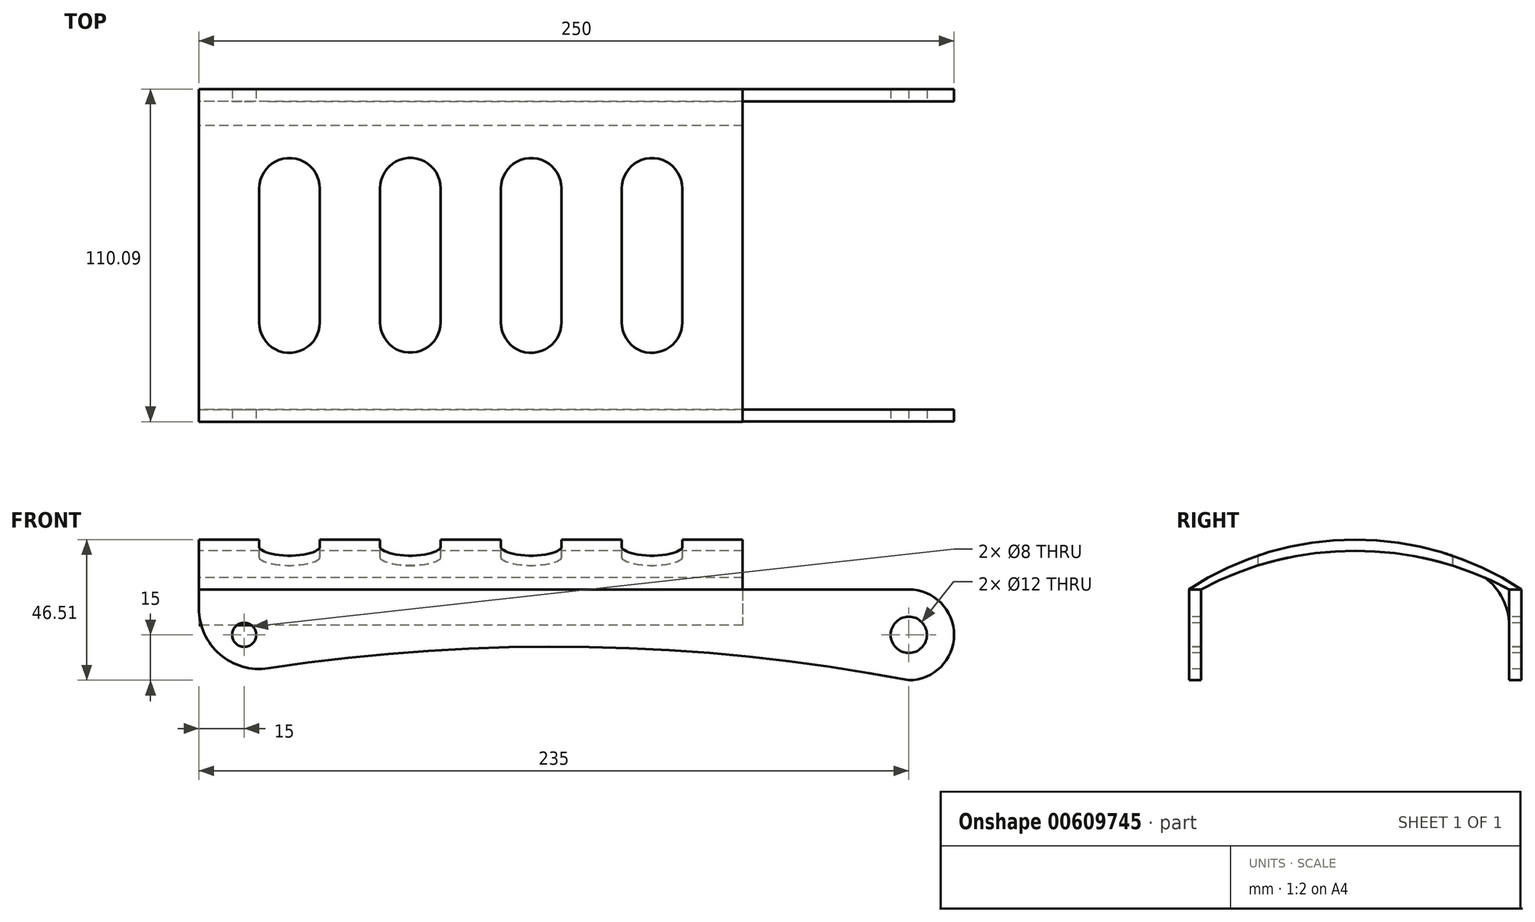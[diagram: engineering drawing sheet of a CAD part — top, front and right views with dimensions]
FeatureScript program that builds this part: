
annotation { "Feature Type Name" : "Feature", "Feature Type Description" : "" }
export const myFeature = defineFeature(function(context is Context, id is Id, definition is map)
    precondition{}
    {
        {
            var Q0;
            Q0=qCreatedBy(makeId("Top.planeOp"),FACE);
            var sketch = newSketch(context, id + "F0", { "sketchPlane" : qUnion([Q0])});
            skLineSegment(sketch, "E0.bottom", {"start": v(-125, 84.4) * mm, "end": v(125, 84.4) * mm});
            skLineSegment(sketch, "E0.top", {"start": v(-125, 80.4) * mm, "end": v(125, 80.4) * mm});
            skLineSegment(sketch, "E0.left", {"start": v(-125, 84.4) * mm, "end": v(-125, 80.4) * mm});
            skLineSegment(sketch, "E0.right", {"start": v(125, 84.4) * mm, "end": v(125, 80.4) * mm});
            skLineSegment(sketch, "E1.bottom", {"start": v(-125, -21.6) * mm, "end": v(125, -21.6) * mm});
            skLineSegment(sketch, "E1.top", {"start": v(-125, -25.6) * mm, "end": v(125, -25.6) * mm});
            skLineSegment(sketch, "E1.left", {"start": v(-125, -21.6) * mm, "end": v(-125, -25.6) * mm});
            skLineSegment(sketch, "E1.right", {"start": v(125, -21.6) * mm, "end": v(125, -25.6) * mm});
            skSolve(sketch);
        }
        {
            var Q0;
            Q0 = qSketchRegion(id + "F0", true);
            extrude(context, id + "F1", {"entities" : qUnion([Q0]), "depth" : 30 * mm, "offsetDistance" : 25 * mm});
        }
        {
            var Q0;
            Q0=makeQuery(id+"F1.opExtrude","SWEPT_FACE",FACE,{"disambiguationData":[OSD([sQuery(id+"F0.wireOp",EDGE,"E1.top")])]});
            var sketch = newSketch(context, id + "F2", { "sketchPlane" : qUnion([Q0])});
            skLineSegment(sketch, "E2", {"start": v(110, 37.38) * mm, "end": v(110, -21.55) * mm, "construction": true});
            skArc(sketch, "E3", {"start": v(110, 0) * mm, "mid": v(125, 15) * mm, "end": v(110, 30) * mm});
            skArc(sketch, "E4", {"start": v(110, 0) * mm, "mid": v(-7.5, 11.09) * mm, "end": v(-125, 0) * mm});
            skArc(sketch, "E5", {"start": v(110, 33) * mm, "mid": v(-7.5, 38.9) * mm, "end": v(-125, 33) * mm});
            skLineSegment(sketch, "E6", {"start": v(-125, 30) * mm, "end": v(-125, 33) * mm});
            skLineSegment(sketch, "E7", {"start": v(110, 33) * mm, "end": v(110, 30) * mm});
            skSolve(sketch);
        }
        {
            var Q0;
            {var subQ0=sQuery(id+"F2.wireOp",EDGE,"E4");Q0=makeQuery(id+"F2.imprint","IMPRINT",FACE,{"disambiguationData":[TD([[makeQuery(id+"F2.imprint","IMPRINT",EDGE,{"derivedFrom":subQ0}),1.0]])]});}
            var Q1;
            {var subQ0=sQuery(id+"F2.wireOp",EDGE,"E3");var subQ1=sQuery(id+"F0.wireOp",EDGE,"E1.top");var subQ2=makeQuery(id+"F1.opExtrude","CAP_EDGE",EDGE,{"disambiguationData":[OSD([subQ1])],"isStart":false});var subQ3=makeQuery(id+"F2.imprint","INTERSECT",VERTEX,{"derivedFrom":[subQ2,subQ0,sQuery(id+"F2.wireOp",EDGE,"E5")]});Q1=makeQuery(id+"F2.imprint","IMPRINT",FACE,{"disambiguationData":[TD([[makeQuery(id+"F2.imprint","IMPRINT",EDGE,{"disambiguationData":[TD([[subQ3,1.0]])],"derivedFrom":subQ0}),-1.0]])]});}
            var Q2;
            {var subQ0=sQuery(id+"F2.wireOp",EDGE,"E3");var subQ1=sQuery(id+"F0.wireOp",EDGE,"E1.top");var subQ2=makeQuery(id+"F1.opExtrude","CAP_EDGE",EDGE,{"disambiguationData":[OSD([subQ1])],"isStart":true});var subQ3=makeQuery(id+"F2.imprint","INTERSECT",VERTEX,{"derivedFrom":[subQ2,subQ0,sQuery(id+"F2.wireOp",EDGE,"E4")]});Q2=makeQuery(id+"F2.imprint","IMPRINT",FACE,{"disambiguationData":[TD([[makeQuery(id+"F2.imprint","IMPRINT",EDGE,{"disambiguationData":[TD([[subQ3,-1.0]])],"derivedFrom":subQ0}),-1.0]])]});}
            extrude(context, id + "F3", {"entities" : qUnion([Q0, Q1, Q2]), "operationType" : NewBodyOperationType.REMOVE, "oppositeDirection" : true, "depth" : 144.6 * mm, "offsetDistance" : 25 * mm});
        }
        {
            var Q0;
            Q0=makeQuery(id+"F1.opExtrude","SWEPT_FACE",FACE,{"disambiguationData":[OSD([sQuery(id+"F0.wireOp",EDGE,"E0.left")])]});
            var sketch = newSketch(context, id + "F4", { "sketchPlane" : qUnion([Q0])});
            skArc(sketch, "E8", {"start": v(21.68, 30) * mm, "mid": v(-29.36, 42.82) * mm, "end": v(-80.4, 30) * mm});
            skArc(sketch, "E9", {"start": v(25.68, 30) * mm, "mid": v(-29.36, 46.51) * mm, "end": v(-84.4, 30) * mm});
            skLineSegment(sketch, "E10", {"start": v(21.68, 30) * mm, "end": v(25.68, 30) * mm});
            skLineSegment(sketch, "E11", {"start": v(-84.4, 30) * mm, "end": v(-80.4, 30) * mm});
            skArc(sketch, "E12", {"start": v(21.6, 18.23) * mm, "mid": v(19.41, 27) * mm, "end": v(13.6, 33.91) * mm});
            skArc(sketch, "E13", {"start": v(-72.4, 33.88) * mm, "mid": v(-78.22, 26.98) * mm, "end": v(-80.4, 18.23) * mm});
            skSolve(sketch);
        }
        {
            var Q0;
            Q0 = qSketchRegion(id + "F4", true);
            extrude(context, id + "F5", {"entities" : qUnion([Q0]), "oppositeDirection" : true, "depth" : 180 * mm, "offsetDistance" : 25 * mm});
        }
        {
            var Q0;
            Q0=qCreatedBy(makeId("Top.planeOp"),FACE);
            var sketch = newSketch(context, id + "F6", { "sketchPlane" : qUnion([Q0])});
            skLineSegment(sketch, "E14.bottom", {"start": v(-95, 61.6) * mm, "end": v(-95, 61.6) * mm});
            skLineSegment(sketch, "E14.top", {"start": v(-95, -2.87) * mm, "end": v(-95, -2.87) * mm});
            skLineSegment(sketch, "E14.left", {"start": v(-105, 51.6) * mm, "end": v(-105, 7.13) * mm});
            skLineSegment(sketch, "E14.right", {"start": v(-85, 51.6) * mm, "end": v(-85, 7.13) * mm});
            skLineSegment(sketch, "E15.bottom", {"start": v(-55, 61.68) * mm, "end": v(-55, 61.68) * mm});
            skLineSegment(sketch, "E15.top", {"start": v(-55, -2.78) * mm, "end": v(-55, -2.78) * mm});
            skLineSegment(sketch, "E15.left", {"start": v(-65, 51.68) * mm, "end": v(-65, 7.22) * mm});
            skLineSegment(sketch, "E15.right", {"start": v(-45, 51.68) * mm, "end": v(-45, 7.22) * mm});
            skLineSegment(sketch, "E16.bottom", {"start": v(-15, 61.6) * mm, "end": v(-15, 61.6) * mm});
            skLineSegment(sketch, "E16.top", {"start": v(-15, -2.87) * mm, "end": v(-15, -2.87) * mm});
            skLineSegment(sketch, "E16.left", {"start": v(-25, 51.6) * mm, "end": v(-25, 7.13) * mm});
            skLineSegment(sketch, "E16.right", {"start": v(-5, 51.6) * mm, "end": v(-5, 7.13) * mm});
            skLineSegment(sketch, "E17.bottom", {"start": v(25, 61.6) * mm, "end": v(25, 61.6) * mm});
            skLineSegment(sketch, "E17.top", {"start": v(25, -2.87) * mm, "end": v(25, -2.87) * mm});
            skLineSegment(sketch, "E17.left", {"start": v(15, 51.6) * mm, "end": v(15, 7.13) * mm});
            skLineSegment(sketch, "E17.right", {"start": v(35, 51.6) * mm, "end": v(35, 7.13) * mm});
            skPoint(sketch, "E18.visualSharp", {"position": v(-105, 61.6) * mm});
            skArc(sketch, "E18.filletArc", {"start": v(-95, 61.6) * mm, "mid": v(-102.07, 58.66) * mm, "end": v(-105, 51.6) * mm});
            skPoint(sketch, "E19.visualSharp", {"position": v(-85, 61.6) * mm});
            skArc(sketch, "E19.filletArc", {"start": v(-85, 51.6) * mm, "mid": v(-87.93, 58.66) * mm, "end": v(-95, 61.6) * mm});
            skPoint(sketch, "E20.visualSharp", {"position": v(-85, -2.87) * mm});
            skArc(sketch, "E20.filletArc", {"start": v(-95, -2.87) * mm, "mid": v(-87.93, 0.06) * mm, "end": v(-85, 7.13) * mm});
            skPoint(sketch, "E21.visualSharp", {"position": v(-105, -2.87) * mm});
            skArc(sketch, "E21.filletArc", {"start": v(-105, 7.13) * mm, "mid": v(-102.07, 0.06) * mm, "end": v(-95, -2.87) * mm});
            skPoint(sketch, "E22.visualSharp", {"position": v(-65, -2.78) * mm});
            skArc(sketch, "E22.filletArc", {"start": v(-65, 7.22) * mm, "mid": v(-62.07, 0.14) * mm, "end": v(-55, -2.78) * mm});
            skPoint(sketch, "E23.visualSharp", {"position": v(-45, -2.78) * mm});
            skArc(sketch, "E23.filletArc", {"start": v(-55, -2.78) * mm, "mid": v(-47.93, 0.14) * mm, "end": v(-45, 7.22) * mm});
            skPoint(sketch, "E24.visualSharp", {"position": v(-45, 61.68) * mm});
            skArc(sketch, "E24.filletArc", {"start": v(-45, 51.68) * mm, "mid": v(-47.93, 58.75) * mm, "end": v(-55, 61.68) * mm});
            skPoint(sketch, "E25.visualSharp", {"position": v(-65, 61.68) * mm});
            skArc(sketch, "E25.filletArc", {"start": v(-55, 61.68) * mm, "mid": v(-62.07, 58.75) * mm, "end": v(-65, 51.68) * mm});
            skPoint(sketch, "E26.visualSharp", {"position": v(-25, 61.6) * mm});
            skArc(sketch, "E26.filletArc", {"start": v(-15, 61.6) * mm, "mid": v(-22.07, 58.66) * mm, "end": v(-25, 51.6) * mm});
            skPoint(sketch, "E27.visualSharp", {"position": v(-5, 61.6) * mm});
            skArc(sketch, "E27.filletArc", {"start": v(-5, 51.6) * mm, "mid": v(-7.93, 58.66) * mm, "end": v(-15, 61.6) * mm});
            skPoint(sketch, "E28.visualSharp", {"position": v(-5, -2.87) * mm});
            skArc(sketch, "E28.filletArc", {"start": v(-15, -2.87) * mm, "mid": v(-7.93, 0.06) * mm, "end": v(-5, 7.13) * mm});
            skPoint(sketch, "E29.visualSharp", {"position": v(-25, -2.87) * mm});
            skArc(sketch, "E29.filletArc", {"start": v(-25, 7.13) * mm, "mid": v(-22.07, 0.06) * mm, "end": v(-15, -2.87) * mm});
            skPoint(sketch, "E30.visualSharp", {"position": v(15, 61.6) * mm});
            skArc(sketch, "E30.filletArc", {"start": v(25, 61.6) * mm, "mid": v(17.93, 58.66) * mm, "end": v(15, 51.6) * mm});
            skPoint(sketch, "E31.visualSharp", {"position": v(35, 61.6) * mm});
            skArc(sketch, "E31.filletArc", {"start": v(35, 51.6) * mm, "mid": v(32.07, 58.66) * mm, "end": v(25, 61.6) * mm});
            skPoint(sketch, "E32.visualSharp", {"position": v(35, -2.87) * mm});
            skArc(sketch, "E32.filletArc", {"start": v(25, -2.87) * mm, "mid": v(32.07, 0.06) * mm, "end": v(35, 7.13) * mm});
            skPoint(sketch, "E33.visualSharp", {"position": v(15, -2.87) * mm});
            skArc(sketch, "E33.filletArc", {"start": v(15, 7.13) * mm, "mid": v(17.93, 0.06) * mm, "end": v(25, -2.87) * mm});
            skSolve(sketch);
        }
        {
            var Q0;
            Q0 = qSketchRegion(id + "F6", true);
            extrude(context, id + "F7", {"entities" : qUnion([Q0]), "operationType" : NewBodyOperationType.REMOVE, "depth" : 70.6 * mm, "offsetDistance" : 25 * mm});
        }
        {
            var Q0;
            Q0=makeQuery(id+"F3.boolean.opBoolean","MERGE",EDGE,{"derivedFrom":[makeQuery(id+"F1.opExtrude","CAP_EDGE",EDGE,{"disambiguationData":[OSD([sQuery(id+"F0.wireOp",EDGE,"E0.left")])],"isStart":true}),makeQuery(id+"F3.opExtrude","SWEPT_EDGE",EDGE,{"disambiguationData":[OSD([sQuery(id+"F0.wireOp",EDGE,"E1.top"),sQuery(id+"F0.wireOp",EDGE,"E1.left"),sQuery(id+"F2.wireOp",EDGE,"E4")])]})]});
            var Q1;
            {var subQ0=sQuery(id+"F0.wireOp",EDGE,"E1.left");Q1=makeQuery(id+"F3.boolean.opBoolean","MERGE",EDGE,{"derivedFrom":[makeQuery(id+"F1.opExtrude","CAP_EDGE",EDGE,{"disambiguationData":[OSD([subQ0])],"isStart":true}),makeQuery(id+"F3.opExtrude","SWEPT_EDGE",EDGE,{"disambiguationData":[OSD([sQuery(id+"F0.wireOp",EDGE,"E1.top"),subQ0,sQuery(id+"F2.wireOp",EDGE,"E4")])]})]});}
            fillet(context, id + "F8", {"entities" : qUnion([Q0, Q1]), "radius" : 20 * mm, "tangentPropagation" : true, "allowEdgeOverflow" : false});
        }
        {
            var Q0;
            Q0=makeQuery(id+"F1.opExtrude","SWEPT_FACE",FACE,{"disambiguationData":[OSD([sQuery(id+"F0.wireOp",EDGE,"E1.top")])]});
            var sketch = newSketch(context, id + "F9", { "sketchPlane" : qUnion([Q0])});
            skCircle(sketch, "E34", {"center": v(-110, 15) * mm, "radius": 4 * mm});
            skSolve(sketch);
        }
        {
            var Q0;
            Q0 = qSketchRegion(id + "F9", true);
            extrude(context, id + "F10", {"entities" : qUnion([Q0]), "operationType" : NewBodyOperationType.REMOVE, "oppositeDirection" : true, "depth" : 169.5 * mm, "offsetDistance" : 25 * mm});
        }
        {
            var Q0;
            Q0=makeQuery(id+"F1.opExtrude","SWEPT_FACE",FACE,{"disambiguationData":[OSD([sQuery(id+"F0.wireOp",EDGE,"E1.top")])]});
            var sketch = newSketch(context, id + "F11", { "sketchPlane" : qUnion([Q0])});
            skCircle(sketch, "E35", {"center": v(110, 15) * mm, "radius": 6 * mm});
            skSolve(sketch);
        }
        {
            var Q0;
            Q0 = qSketchRegion(id + "F11", true);
            extrude(context, id + "F12", {"entities" : qUnion([Q0]), "operationType" : NewBodyOperationType.REMOVE, "oppositeDirection" : true, "depth" : 143.3 * mm, "offsetDistance" : 25 * mm});
        }
        {
            var Q0;
            {var subQ3=sQuery(id+"F4.wireOp",EDGE,"E13");Q0=makeQuery(id+"F4.imprint","IMPRINT",FACE,{"disambiguationData":[TD([[makeQuery(id+"F4.imprint","IMPRINT",EDGE,{"derivedFrom":subQ3}),-1.0]])]});}
            extrude(context, id + "F13", {"entities" : qUnion([Q0]), "oppositeDirection" : true, "depth" : 180 * mm, "offsetDistance" : 25 * mm});
        }
    });
